# Revit family: 210_CAD O Integral ER 25 VLD
name_source: partatom
category: Mechanical Equipment
units: mm (PartAtom-declared; Revit-internal decimal feet)

## family parameters
Always vertical = Yes
Cut with Voids When Loaded = No
Part Type = Breaks Into
Room Calculation Point = No
Round Connector Dimension = Use Diameter
Shared = No
Work Plane-Based = No

## types (1)
- CAD O Integral ER 25 VLD
    AA1 = 779 mm  [stored 2.55577 ft]
    AA2 = 779 mm  [stored 2.55577 ft]
    AA3 = 59 mm
    AA3__ve = -59 mm
    AA4 = 838 mm
    BB1 = 483 mm  [stored 1.58465 ft]
    CAT0 = Yes
    D = 400 mm
    HH1 = 1183 mm  [stored 3.88123 ft]
    Manufacturer = VIM
    QmdConnectorList = 221;D;231;D;241;D;251;D
    R = 200 mm  [stored 0.656168 ft]
    SPG = 379 mm  [stored 1.24344 ft]
    SPH = 904 mm  [stored 2.96588 ft]
    SPI1 = 483 mm  [stored 1.58465 ft]
    SPI2 = 483 mm  [stored 1.58465 ft]
    W = 500 mm
    magiPartTypeId = 210
    magiProductCode = CAD O Integral ER 25 VLD
    magiProductFamilyId = CAD O Integral ER 25 VLD
    magiProductId = CAD O Integral ER 25 VLD

note: [stored X ft] marks values corroborated as IEEE doubles in the binary element streams (Revit-internal decimal feet)

## geometry (parser evidence)
native form markers: Sweep x2
no freeform markers — native parametric forms only
